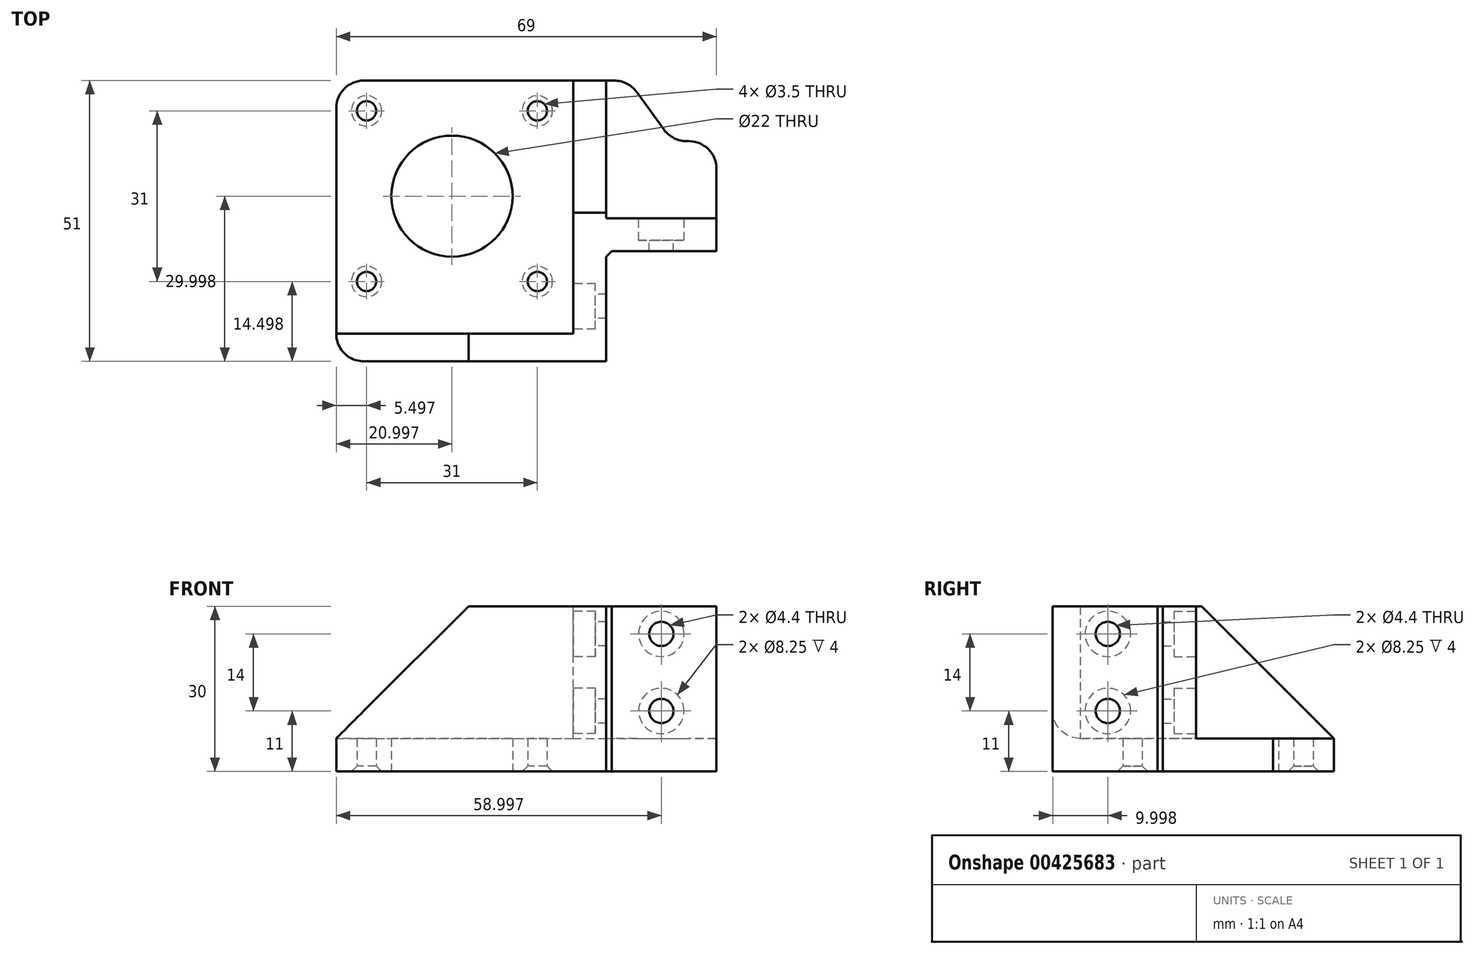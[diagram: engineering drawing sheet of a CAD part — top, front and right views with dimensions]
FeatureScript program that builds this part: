
annotation { "Feature Type Name" : "Feature", "Feature Type Description" : "" }
export const myFeature = defineFeature(function(context is Context, id is Id, definition is map)
    precondition{}
    {
        {
            var Q0;
            Q0=qCreatedBy(makeId("Top.planeOp"),FACE);
            var sketch = newSketch(context, id + "F0", { "sketchPlane" : qUnion([Q0])});
            skLineSegment(sketch, "E0.bottom", {"start": v(-30.12, 25.58) * mm, "end": v(18.88, 25.58) * mm});
            skLineSegment(sketch, "E0.top", {"start": v(-30.12, -25.42) * mm, "end": v(18.88, -25.42) * mm});
            skLineSegment(sketch, "E0.left", {"start": v(-30.12, 25.58) * mm, "end": v(-30.12, -25.42) * mm});
            skLineSegment(sketch, "E0.right", {"start": v(18.88, 25.58) * mm, "end": v(18.88, -25.42) * mm});
            skLineSegment(sketch, "E1", {"start": v(-51.12, -5.42) * mm, "end": v(63.52, -5.42) * mm, "construction": true});
            skLineSegment(sketch, "E2", {"start": v(-50.26, 14.58) * mm, "end": v(65.58, 14.58) * mm, "construction": true});
            skLineSegment(sketch, "E3", {"start": v(30.88, 48.45) * mm, "end": v(30.88, -32.1) * mm, "construction": true});
            skLineSegment(sketch, "E4", {"start": v(22.88, 49.32) * mm, "end": v(22.88, -46.56) * mm, "construction": true});
            skLineSegment(sketch, "E5", {"start": v(18.88, 25.58) * mm, "end": v(22.88, 25.58) * mm});
            skLineSegment(sketch, "E6", {"start": v(22.88, 25.58) * mm, "end": v(30.88, 14.58) * mm});
            skLineSegment(sketch, "E7", {"start": v(30.88, 14.58) * mm, "end": v(38.88, 14.58) * mm});
            skLineSegment(sketch, "E8", {"start": v(38.88, 14.58) * mm, "end": v(38.88, -5.42) * mm});
            skLineSegment(sketch, "E9", {"start": v(38.88, -5.42) * mm, "end": v(18.88, -5.42) * mm});
            skCircle(sketch, "E10", {"center": v(-9.12, 4.58) * mm, "radius": 11 * mm});
            skCircle(sketch, "E11", {"center": v(-24.62, 20.08) * mm, "radius": 1.75 * mm});
            skLineSegment(sketch, "E12", {"start": v(-24.62, 20.08) * mm, "end": v(6.38, 20.08) * mm, "construction": true});
            skLineSegment(sketch, "E13", {"start": v(6.38, 20.08) * mm, "end": v(6.38, -10.92) * mm, "construction": true});
            skLineSegment(sketch, "E14", {"start": v(6.38, -10.92) * mm, "end": v(-24.62, -10.92) * mm, "construction": true});
            skLineSegment(sketch, "E15", {"start": v(-24.62, -10.92) * mm, "end": v(-24.62, 20.08) * mm, "construction": true});
            skCircle(sketch, "E16", {"center": v(6.38, 20.08) * mm, "radius": 1.75 * mm});
            skCircle(sketch, "E17", {"center": v(6.38, -10.92) * mm, "radius": 1.75 * mm});
            skCircle(sketch, "E18", {"center": v(-24.62, -10.92) * mm, "radius": 1.75 * mm});
            skSolve(sketch);
        }
        {
            var Q0;
            {var subQ1=sQuery(id+"F0.wireOp",EDGE,"E0.bottom");Q0=makeQuery(id+"F0.imprint","IMPRINT",FACE,{"disambiguationData":[TD([[makeQuery(id+"F0.imprint","IMPRINT",EDGE,{"derivedFrom":subQ1}),-1.0]])]});}
            var Q1;
            {var subQ0=sQuery(id+"F0.wireOp",EDGE,"E5");Q1=makeQuery(id+"F0.imprint","IMPRINT",FACE,{"disambiguationData":[TD([[makeQuery(id+"F0.imprint","IMPRINT",EDGE,{"derivedFrom":subQ0}),-1.0]])]});}
            extrude(context, id + "F1", {"entities" : qUnion([Q0, Q1]), "depth" : 6 * mm, "offsetDistance" : 25 * mm});
        }
        {
            var Q0;
            Q0=makeQuery(id+"F1.opExtrude","CAP_EDGE",EDGE,{"disambiguationData":[OSD([sQuery(id+"F0.wireOp",EDGE,"E11")])],"isStart":true});
            var Q1;
            Q1=makeQuery(id+"F1.opExtrude","CAP_EDGE",EDGE,{"disambiguationData":[OSD([sQuery(id+"F0.wireOp",EDGE,"E16")])],"isStart":true});
            var Q2;
            Q2=makeQuery(id+"F1.opExtrude","CAP_EDGE",EDGE,{"disambiguationData":[OSD([sQuery(id+"F0.wireOp",EDGE,"E17")])],"isStart":true});
            var Q3;
            Q3=makeQuery(id+"F1.opExtrude","CAP_EDGE",EDGE,{"disambiguationData":[OSD([sQuery(id+"F0.wireOp",EDGE,"E18")])],"isStart":true});
            chamfer(context, id + "F2", {"entities" : qUnion([Q0, Q1, Q2, Q3]), "width" : 1 * mm, "tangentPropagation" : true});
        }
        {
            var Q0;
            Q0=makeQuery(id+"F1.opExtrude","CAP_FACE",FACE,{"disambiguationData":[OSD([sQuery(id+"F0.wireOp",EDGE,"E0.bottom"),sQuery(id+"F0.wireOp",EDGE,"E0.top"),sQuery(id+"F0.wireOp",EDGE,"E0.left"),sQuery(id+"F0.wireOp",EDGE,"E0.right"),sQuery(id+"F0.wireOp",EDGE,"E5"),sQuery(id+"F0.wireOp",EDGE,"E6"),sQuery(id+"F0.wireOp",EDGE,"E7"),sQuery(id+"F0.wireOp",EDGE,"E8"),sQuery(id+"F0.wireOp",EDGE,"E9"),sQuery(id+"F0.wireOp",EDGE,"E10"),sQuery(id+"F0.wireOp",EDGE,"E11"),sQuery(id+"F0.wireOp",EDGE,"E16"),sQuery(id+"F0.wireOp",EDGE,"E17"),sQuery(id+"F0.wireOp",EDGE,"E18")])],"isStart":false});
            var sketch = newSketch(context, id + "F3", { "sketchPlane" : qUnion([Q0])});
            skLineSegment(sketch, "E19.bottom", {"start": v(18.88, -5.42) * mm, "end": v(38.88, -5.42) * mm});
            skLineSegment(sketch, "E19.top", {"start": v(12.88, 0.58) * mm, "end": v(38.88, 0.58) * mm});
            skLineSegment(sketch, "E19.left", {"start": v(12.88, -25.42) * mm, "end": v(12.88, 0.58) * mm});
            skLineSegment(sketch, "E19.right", {"start": v(38.88, -5.42) * mm, "end": v(38.88, 0.58) * mm});
            skLineSegment(sketch, "E20.bottom", {"start": v(18.88, -25.42) * mm, "end": v(12.88, -25.42) * mm});
            skLineSegment(sketch, "E20.left", {"start": v(18.88, -25.42) * mm, "end": v(18.88, -5.42) * mm});
            skSolve(sketch);
        }
        {
            var Q0;
            Q0=makeQuery(id+"F3.imprint","IMPRINT",FACE,{"disambiguationData":[TD([[makeQuery(id+"F3.imprint","IMPRINT",EDGE,{"derivedFrom":sQuery(id+"F3.wireOp",EDGE,"E19.bottom")}),-1.0]])]});
            extrude(context, id + "F4", {"entities" : qUnion([Q0]), "operationType" : NewBodyOperationType.ADD, "depth" : 24 * mm, "offsetDistance" : 25 * mm});
        }
        {
            var Q0;
            Q0=makeQuery(id+"F3.imprint","IMPRINT",FACE,{"disambiguationData":[TD([[makeQuery(id+"F3.imprint","IMPRINT",EDGE,{"derivedFrom":sQuery(id+"F3.wireOp",EDGE,"E20.bottom")}),1.0]])]});
            extrude(context, id + "F5", {"entities" : qUnion([Q0]), "operationType" : NewBodyOperationType.ADD, "depth" : 10 * mm, "offsetDistance" : 25 * mm});
        }
        {
            var Q0;
            Q0=makeQuery(id+"F1.opExtrude","SWEPT_EDGE",EDGE,{"disambiguationData":[OSD([sQuery(id+"F0.wireOp",EDGE,"E0.right"),sQuery(id+"F0.wireOp",EDGE,"E9")])]});
            chamfer(context, id + "F6", {"entities" : qUnion([Q0]), "width" : 1 * mm, "tangentPropagation" : true});
        }
        {
            var Q0;
            Q0=makeQuery(id+"F4.opExtrude","SWEPT_FACE",FACE,{"disambiguationData":[OSD([sQuery(id+"F3.wireOp",EDGE,"E19.top")])]});
            var sketch = newSketch(context, id + "F7", { "sketchPlane" : qUnion([Q0])});
            skLineSegment(sketch, "E21", {"start": v(-28.88, 30) * mm, "end": v(-28.88, 12) * mm, "construction": true});
            skPoint(sketch, "E22", {"position": v(-28.88, 11) * mm});
            skPoint(sketch, "E23", {"position": v(-28.88, 25) * mm});
            skSolve(sketch);
        }
        {
            var Q0;
            Q0=sQuery(id+"F7.wireOp",VERTEX,"E23");
            var Q1;
            Q1=sQuery(id+"F7.wireOp",VERTEX,"E22");
            var Q2;
            Q2=makeQuery(id+"F1.opExtrude","SWEPT_BODY",BODY,{"disambiguationData":[OSD([sQuery(id+"F0.wireOp",EDGE,"E0.bottom"),sQuery(id+"F0.wireOp",EDGE,"E0.top"),sQuery(id+"F0.wireOp",EDGE,"E0.left"),sQuery(id+"F0.wireOp",EDGE,"E0.right"),sQuery(id+"F0.wireOp",EDGE,"E5"),sQuery(id+"F0.wireOp",EDGE,"E6"),sQuery(id+"F0.wireOp",EDGE,"E7"),sQuery(id+"F0.wireOp",EDGE,"E8"),sQuery(id+"F0.wireOp",EDGE,"E9"),sQuery(id+"F0.wireOp",EDGE,"E10"),sQuery(id+"F0.wireOp",EDGE,"E11"),sQuery(id+"F0.wireOp",EDGE,"E16"),sQuery(id+"F0.wireOp",EDGE,"E17"),sQuery(id+"F0.wireOp",EDGE,"E18")])]});
            hole(context, id + "F8", {"style" : HoleStyle.C_BORE, "endStyle" : HoleEndStyle.THROUGH, "standardTappedOrClearance" : lookupTablePath({ "standard" : "ISO", "fit" : "Normal", "size" : "M4", "type" : "Clearance" }), "standardBlindInLast" : lookupTablePath({ "fit" : "Standard", "standard" : "ISO", "size" : "M4", "type" : "Clearance" }), "holeDiameter" : 4.4 * mm, "cBoreDiameter" : 8.25 * mm, "cBoreDepth" : 4 * mm, "majorDiameter" : 5 * mm, "isTappedThrough" : true, "tappedDepth" : 12 * mm, "tapClearance" : 3, "locations" : qUnion([Q0, Q1]), "scope" : qUnion([Q2])});
        }
        {
            var Q0;
            Q0=makeQuery(id+"F4.opExtrude","SWEPT_FACE",FACE,{"disambiguationData":[OSD([sQuery(id+"F3.wireOp",EDGE,"E19.left")])]});
            var sketch = newSketch(context, id + "F9", { "sketchPlane" : qUnion([Q0])});
            skPoint(sketch, "E24", {"position": v(15.42, 25) * mm});
            skPoint(sketch, "E25", {"position": v(15.42, 11) * mm});
            skLineSegment(sketch, "E26", {"start": v(15.42, 30) * mm, "end": v(15.42, 6) * mm, "construction": true});
            skSolve(sketch);
        }
        {
            var Q0;
            Q0=sQuery(id+"F9.wireOp",VERTEX,"E24");
            var Q1;
            Q1=sQuery(id+"F9.wireOp",VERTEX,"E25");
            var Q2;
            Q2=makeQuery(id+"F1.opExtrude","SWEPT_BODY",BODY,{"disambiguationData":[OSD([sQuery(id+"F0.wireOp",EDGE,"E0.bottom"),sQuery(id+"F0.wireOp",EDGE,"E0.top"),sQuery(id+"F0.wireOp",EDGE,"E0.left"),sQuery(id+"F0.wireOp",EDGE,"E0.right"),sQuery(id+"F0.wireOp",EDGE,"E5"),sQuery(id+"F0.wireOp",EDGE,"E6"),sQuery(id+"F0.wireOp",EDGE,"E7"),sQuery(id+"F0.wireOp",EDGE,"E8"),sQuery(id+"F0.wireOp",EDGE,"E9"),sQuery(id+"F0.wireOp",EDGE,"E10"),sQuery(id+"F0.wireOp",EDGE,"E11"),sQuery(id+"F0.wireOp",EDGE,"E16"),sQuery(id+"F0.wireOp",EDGE,"E17"),sQuery(id+"F0.wireOp",EDGE,"E18")])]});
            hole(context, id + "F10", {"style" : HoleStyle.C_BORE, "endStyle" : HoleEndStyle.THROUGH, "standardTappedOrClearance" : lookupTablePath({ "standard" : "ISO", "fit" : "Normal", "size" : "M4", "type" : "Clearance" }), "standardBlindInLast" : lookupTablePath({ "fit" : "Standard", "standard" : "ISO", "size" : "M4", "type" : "Clearance" }), "holeDiameter" : 4.4 * mm, "cBoreDiameter" : 8.25 * mm, "cBoreDepth" : 4 * mm, "majorDiameter" : 5 * mm, "isTappedThrough" : true, "tappedDepth" : 12 * mm, "tapClearance" : 3, "locations" : qUnion([Q0, Q1]), "scope" : qUnion([Q2])});
        }
        {
            var Q0;
            Q0=makeQuery(id+"F4.opExtrude","SWEPT_FACE",FACE,{"disambiguationData":[OSD([sQuery(id+"F3.wireOp",EDGE,"E19.top")])]});
            var sketch = newSketch(context, id + "F11", { "sketchPlane" : qUnion([Q0])});
            skLineSegment(sketch, "E27.bottom", {"start": v(-12.88, 30) * mm, "end": v(-18.88, 30) * mm});
            skLineSegment(sketch, "E27.top", {"start": v(-12.88, 6) * mm, "end": v(-18.88, 6) * mm});
            skLineSegment(sketch, "E27.left", {"start": v(-12.88, 30) * mm, "end": v(-12.88, 6) * mm});
            skLineSegment(sketch, "E27.right", {"start": v(-18.88, 30) * mm, "end": v(-18.88, 6) * mm});
            skSolve(sketch);
        }
        {
            var Q0;
            Q0=makeQuery(id+"F11.imprint","IMPRINT",FACE,{"disambiguationData":[TD([[makeQuery(id+"F11.imprint","IMPRINT",EDGE,{"derivedFrom":sQuery(id+"F11.wireOp",EDGE,"E27.bottom")}),1.0]])]});
            var Q1;
            Q1=makeQuery(id+"F1.opExtrude","SWEPT_FACE",FACE,{"disambiguationData":[OSD([sQuery(id+"F0.wireOp",EDGE,"E0.bottom"),sQuery(id+"F0.wireOp",EDGE,"E5")])]});
            extrude(context, id + "F12", {"entities" : qUnion([Q0]), "operationType" : NewBodyOperationType.ADD, "endBound" : BoundingType.UP_TO_SURFACE, "depth" : 25 * mm, "endBoundEntityFace" : qUnion([Q1]), "offsetDistance" : 25 * mm});
        }
        {
            var Q0;
            Q0=makeQuery(id+"F12.boolean.opBoolean","MERGE",FACE,{"derivedFrom":[makeQuery(id+"F4.opExtrude","SWEPT_FACE",FACE,{"disambiguationData":[OSD([sQuery(id+"F3.wireOp",EDGE,"E19.left")])]}),makeQuery(id+"F12.opExtrude","SWEPT_FACE",FACE,{"disambiguationData":[OSD([sQuery(id+"F11.wireOp",EDGE,"E27.left")])]})]});
            var sketch = newSketch(context, id + "F13", { "sketchPlane" : qUnion([Q0])});
            skLineSegment(sketch, "E28.bottom", {"start": v(25.42, 30) * mm, "end": v(20.42, 30) * mm});
            skLineSegment(sketch, "E28.top", {"start": v(25.42, 6) * mm, "end": v(20.42, 6) * mm});
            skLineSegment(sketch, "E28.left", {"start": v(25.42, 30) * mm, "end": v(25.42, 6) * mm});
            skLineSegment(sketch, "E28.right", {"start": v(20.42, 30) * mm, "end": v(20.42, 6) * mm});
            skSolve(sketch);
        }
        {
            var Q0;
            Q0 = qSketchRegion(id + "F13", true);
            var Q1;
            Q1=makeQuery(id+"F1.opExtrude","SWEPT_FACE",FACE,{"disambiguationData":[OSD([sQuery(id+"F0.wireOp",EDGE,"E0.left")])]});
            extrude(context, id + "F14", {"entities" : qUnion([Q0]), "operationType" : NewBodyOperationType.ADD, "endBound" : BoundingType.UP_TO_SURFACE, "depth" : 25 * mm, "endBoundEntityFace" : qUnion([Q1]), "offsetDistance" : 25 * mm});
        }
        {
            var Q0;
            Q0=makeQuery(id+"F14.opExtrude","CAP_EDGE",EDGE,{"disambiguationData":[OSD([sQuery(id+"F13.wireOp",EDGE,"E28.bottom")])],"isStart":false});
            var Q1;
            Q1=makeQuery(id+"F12.opExtrude","CAP_EDGE",EDGE,{"disambiguationData":[OSD([sQuery(id+"F11.wireOp",EDGE,"E27.bottom")])],"isStart":false});
            chamfer(context, id + "F15", {"entities" : qUnion([Q0, Q1]), "width" : 24 * mm, "tangentPropagation" : true});
        }
        {
            var Q0;
            Q0=makeQuery(id+"F1.opExtrude","SWEPT_EDGE",EDGE,{"disambiguationData":[OSD([sQuery(id+"F0.wireOp",EDGE,"E6"),sQuery(id+"F0.wireOp",EDGE,"E7")])]});
            var Q1;
            Q1=makeQuery(id+"F1.opExtrude","SWEPT_EDGE",EDGE,{"disambiguationData":[OSD([sQuery(id+"F0.wireOp",EDGE,"E5"),sQuery(id+"F0.wireOp",EDGE,"E6")])]});
            var Q2;
            Q2=makeQuery(id+"F1.opExtrude","SWEPT_EDGE",EDGE,{"disambiguationData":[OSD([sQuery(id+"F0.wireOp",EDGE,"E7"),sQuery(id+"F0.wireOp",EDGE,"E8")])]});
            var Q3;
            Q3=makeQuery(id+"F1.opExtrude","SWEPT_EDGE",EDGE,{"disambiguationData":[OSD([sQuery(id+"F0.wireOp",EDGE,"E0.top"),sQuery(id+"F0.wireOp",EDGE,"E0.left")])]});
            var Q4;
            Q4=makeQuery(id+"F1.opExtrude","SWEPT_EDGE",EDGE,{"disambiguationData":[OSD([sQuery(id+"F0.wireOp",EDGE,"E0.bottom"),sQuery(id+"F0.wireOp",EDGE,"E0.left")])]});
            fillet(context, id + "F16", {"entities" : qUnion([Q0, Q1, Q2, Q3, Q4]), "radius" : 5 * mm, "tangentPropagation" : true, "allowEdgeOverflow" : false});
        }
    });
